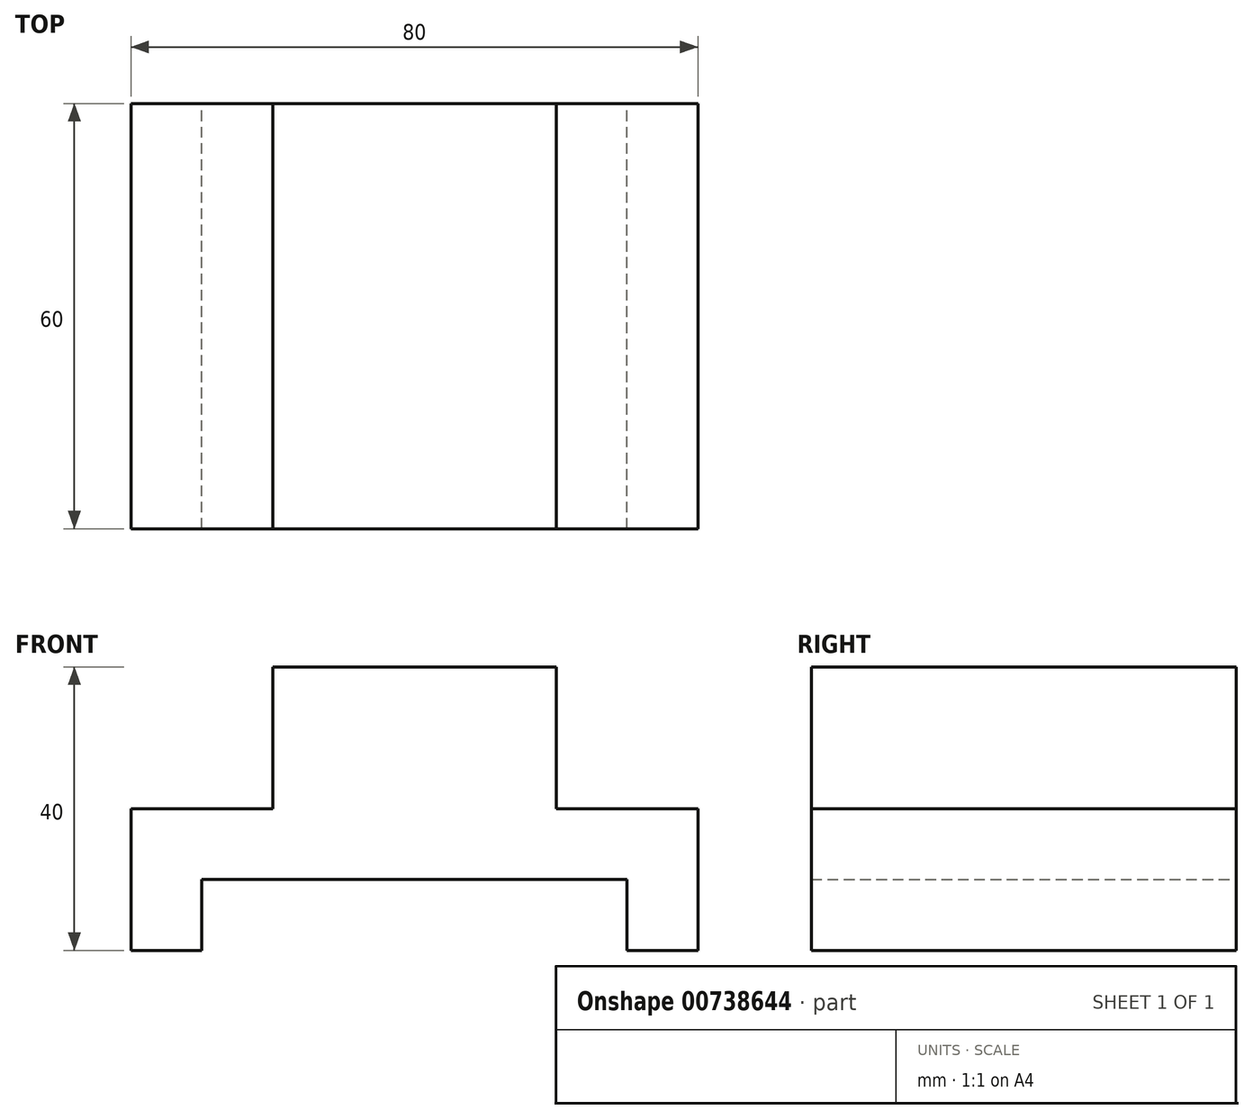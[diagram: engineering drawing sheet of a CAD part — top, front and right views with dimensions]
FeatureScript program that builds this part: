
annotation { "Feature Type Name" : "Feature", "Feature Type Description" : "" }
export const myFeature = defineFeature(function(context is Context, id is Id, definition is map)
    precondition{}
    {
        {
            var Q0;
            Q0=qCreatedBy(makeId("Front.planeOp"),FACE);
            var sketch = newSketch(context, id + "F0", { "sketchPlane" : qUnion([Q0])});
            skLineSegment(sketch, "E0.bottom", {"start": v(0, 0) * mm, "end": v(40, 0) * mm});
            skLineSegment(sketch, "E0.top", {"start": v(0, 30) * mm, "end": v(40, 30) * mm});
            skLineSegment(sketch, "E0.left", {"start": v(0, 0) * mm, "end": v(0, 30) * mm});
            skLineSegment(sketch, "E0.right", {"start": v(40, 0) * mm, "end": v(40, 30) * mm});
            skLineSegment(sketch, "E1.bottom", {"start": v(0, 0) * mm, "end": v(-20, 0) * mm});
            skLineSegment(sketch, "E1.top", {"start": v(0, 10) * mm, "end": v(-20, 10) * mm});
            skLineSegment(sketch, "E1.left", {"start": v(0, 0) * mm, "end": v(0, 10) * mm});
            skLineSegment(sketch, "E1.right", {"start": v(-20, 0) * mm, "end": v(-20, 10) * mm});
            skLineSegment(sketch, "E2.bottom", {"start": v(-20, 0) * mm, "end": v(-10, 0) * mm});
            skLineSegment(sketch, "E2.top", {"start": v(-20, -10) * mm, "end": v(-10, -10) * mm});
            skLineSegment(sketch, "E2.left", {"start": v(-20, 0) * mm, "end": v(-20, -10) * mm});
            skLineSegment(sketch, "E2.right", {"start": v(-10, 0) * mm, "end": v(-10, -10) * mm});
            skLineSegment(sketch, "E3.bottom", {"start": v(40, 0) * mm, "end": v(60, 0) * mm});
            skLineSegment(sketch, "E3.top", {"start": v(40, 10) * mm, "end": v(60, 10) * mm});
            skLineSegment(sketch, "E3.left", {"start": v(40, 0) * mm, "end": v(40, 10) * mm});
            skLineSegment(sketch, "E3.right", {"start": v(60, 0) * mm, "end": v(60, 10) * mm});
            skLineSegment(sketch, "E4.bottom", {"start": v(60, 0) * mm, "end": v(50, 0) * mm});
            skLineSegment(sketch, "E4.top", {"start": v(60, -10) * mm, "end": v(50, -10) * mm});
            skLineSegment(sketch, "E4.left", {"start": v(60, 0) * mm, "end": v(60, -10) * mm});
            skLineSegment(sketch, "E4.right", {"start": v(50, 0) * mm, "end": v(50, -10) * mm});
            skSolve(sketch);
        }
        {
            var Q0;
            Q0 = qSketchRegion(id + "F0", true);
            extrude(context, id + "F1", {"entities" : qUnion([Q0]), "depth" : 60 * mm, "offsetDistance" : 25 * mm});
        }
    });
